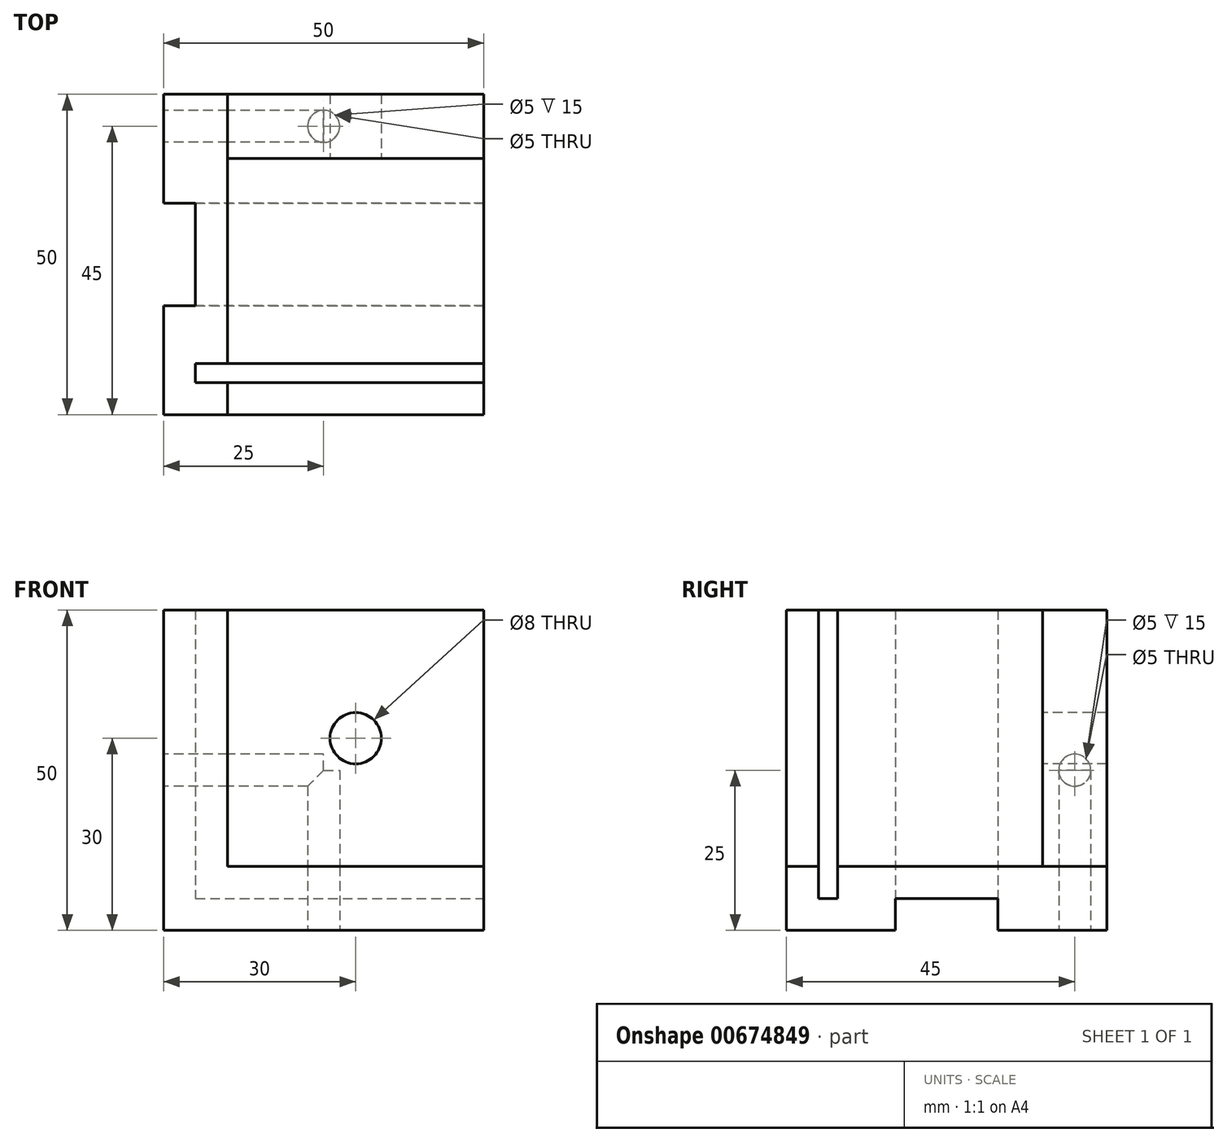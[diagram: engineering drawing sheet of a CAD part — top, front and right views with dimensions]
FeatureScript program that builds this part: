
annotation { "Feature Type Name" : "Feature", "Feature Type Description" : "" }
export const myFeature = defineFeature(function(context is Context, id is Id, definition is map)
    precondition{}
    {
        {
            var Q0;
            Q0=qCreatedBy(makeId("Front.planeOp"),FACE);
            var sketch = newSketch(context, id + "F0", { "sketchPlane" : qUnion([Q0])});
            skLineSegment(sketch, "E0", {"start": v(0, 0) * mm, "end": v(0, 50) * mm});
            skLineSegment(sketch, "E1", {"start": v(0, 50) * mm, "end": v(10, 50) * mm});
            skLineSegment(sketch, "E2", {"start": v(10, 50) * mm, "end": v(10, 10) * mm});
            skLineSegment(sketch, "E3", {"start": v(10, 10) * mm, "end": v(50, 10) * mm});
            skLineSegment(sketch, "E4", {"start": v(50, 10) * mm, "end": v(50, 0) * mm});
            skLineSegment(sketch, "E5", {"start": v(50, 0) * mm, "end": v(0, 0) * mm});
            skSolve(sketch);
        }
        {
            var Q0;
            Q0=makeQuery(id+"F0.imprint","IMPRINT",FACE,{"disambiguationData":[TD([[makeQuery(id+"F0.imprint","IMPRINT",EDGE,{"derivedFrom":sQuery(id+"F0.wireOp",EDGE,"E0")}),-1.0]])]});
            extrude(context, id + "F1", {"entities" : qUnion([Q0]), "depth" : 50 * mm, "offsetDistance" : 25 * mm});
        }
        {
            var Q0;
            Q0=makeQuery(id+"F1.opExtrude","SWEPT_FACE",FACE,{"disambiguationData":[OSD([sQuery(id+"F0.wireOp",EDGE,"E2")])]});
            var sketch = newSketch(context, id + "F2", { "sketchPlane" : qUnion([Q0])});
            skLineSegment(sketch, "E6", {"start": v(-45, 50) * mm, "end": v(-45, 10) * mm});
            skLineSegment(sketch, "E7", {"start": v(-45, 10) * mm, "end": v(-42, 10) * mm});
            skLineSegment(sketch, "E8", {"start": v(-42, 10) * mm, "end": v(-42, 50) * mm});
            skLineSegment(sketch, "E9", {"start": v(-45, 50) * mm, "end": v(-42, 50) * mm});
            skSolve(sketch);
        }
        {
            var Q0;
            Q0=makeQuery(id+"F2.imprint","IMPRINT",FACE,{"disambiguationData":[TD([[makeQuery(id+"F2.imprint","IMPRINT",EDGE,{"derivedFrom":sQuery(id+"F2.wireOp",EDGE,"E6")}),1.0]])]});
            extrude(context, id + "F3", {"entities" : qUnion([Q0]), "operationType" : NewBodyOperationType.REMOVE, "depth" : -5 * mm, "offsetDistance" : 25 * mm});
        }
        {
            var Q0;
            Q0=makeQuery(id+"F3.boolean.opBoolean","MERGE",FACE,{"derivedFrom":[makeQuery(id+"F1.opExtrude","SWEPT_FACE",FACE,{"disambiguationData":[OSD([sQuery(id+"F0.wireOp",EDGE,"E3")])]}),makeQuery(id+"F3.opExtrude","SWEPT_FACE",FACE,{"disambiguationData":[OSD([sQuery(id+"F2.wireOp",EDGE,"E7")])]})]});
            var sketch = newSketch(context, id + "F4", { "sketchPlane" : qUnion([Q0])});
            skLineSegment(sketch, "E10", {"start": v(10, -45) * mm, "end": v(50, -45) * mm});
            skLineSegment(sketch, "E11", {"start": v(50, -45) * mm, "end": v(50, -42) * mm});
            skLineSegment(sketch, "E12", {"start": v(50, -42) * mm, "end": v(10, -42) * mm});
            skSolve(sketch);
        }
        {
            var Q0;
            Q0=makeQuery(id+"F4.imprint","IMPRINT",FACE,{"disambiguationData":[TD([[makeQuery(id+"F4.imprint","IMPRINT",EDGE,{"derivedFrom":sQuery(id+"F4.wireOp",EDGE,"E10")}),1.0]])]});
            extrude(context, id + "F5", {"entities" : qUnion([Q0]), "operationType" : NewBodyOperationType.REMOVE, "oppositeDirection" : true, "depth" : 5 * mm, "offsetDistance" : 25 * mm});
        }
        {
            var Q0;
            Q0=makeQuery(id+"F1.opExtrude","CAP_FACE",FACE,{"disambiguationData":[OSD([sQuery(id+"F0.wireOp",EDGE,"E0"),sQuery(id+"F0.wireOp",EDGE,"E1"),sQuery(id+"F0.wireOp",EDGE,"E2"),sQuery(id+"F0.wireOp",EDGE,"E3"),sQuery(id+"F0.wireOp",EDGE,"E4"),sQuery(id+"F0.wireOp",EDGE,"E5")])],"isStart":true});
            var sketch = newSketch(context, id + "F6", { "sketchPlane" : qUnion([Q0])});
            skLineSegment(sketch, "E13", {"start": v(-10, 50) * mm, "end": v(-50, 50) * mm});
            skLineSegment(sketch, "E14", {"start": v(-50, 50) * mm, "end": v(-50, 10) * mm});
            skSolve(sketch);
        }
        {
            var Q0;
            Q0=makeQuery(id+"F6.imprint","IMPRINT",FACE,{"disambiguationData":[TD([[makeQuery(id+"F6.imprint","IMPRINT",EDGE,{"derivedFrom":sQuery(id+"F6.wireOp",EDGE,"E13")}),1.0]])]});
            extrude(context, id + "F7", {"entities" : qUnion([Q0]), "depth" : -10 * mm, "offsetDistance" : 25 * mm});
        }
        {
            var Q0;
            Q0=makeQuery(id+"F7.opExtrude","CAP_FACE",FACE,{"disambiguationData":[OSD([sQuery(id+"F0.wireOp",EDGE,"E2"),sQuery(id+"F0.wireOp",EDGE,"E3"),sQuery(id+"F6.wireOp",EDGE,"E13"),sQuery(id+"F6.wireOp",EDGE,"E14")])],"isStart":false});
            var sketch = newSketch(context, id + "F8", { "sketchPlane" : qUnion([Q0])});
            skLineSegment(sketch, "E15", {"start": v(10, 50) * mm, "end": v(50, 10) * mm, "construction": true});
            skLineSegment(sketch, "E16", {"start": v(50, 10) * mm, "end": v(50, 50) * mm, "construction": true});
            skLineSegment(sketch, "E17", {"start": v(50, 50) * mm, "end": v(10, 10) * mm, "construction": true});
            skCircle(sketch, "E18", {"center": v(30, 30) * mm, "radius": 4 * mm});
            skCircle(sketch, "E19", {"center": v(30, 30) * mm, "radius": 5 * mm});
            skSolve(sketch);
        }
        {
            var Q0;
            Q0=makeQuery(id+"F8.imprint","IMPRINT",FACE,{"disambiguationData":[TD([[makeQuery(id+"F8.imprint","IMPRINT",EDGE,{"derivedFrom":sQuery(id+"F8.wireOp",EDGE,"E18")}),1.0]])]});
            extrude(context, id + "F9", {"entities" : qUnion([Q0]), "operationType" : NewBodyOperationType.REMOVE, "oppositeDirection" : true, "depth" : 10 * mm, "offsetDistance" : 25 * mm});
        }
        {
            var Q0;
            Q0=makeQuery(id+"F1.opExtrude","SWEPT_FACE",FACE,{"disambiguationData":[OSD([sQuery(id+"F0.wireOp",EDGE,"E0")])]});
            var sketch = newSketch(context, id + "F10", { "sketchPlane" : qUnion([Q0])});
            skLineSegment(sketch, "E20", {"start": v(17, 50) * mm, "end": v(17, 0) * mm});
            skLineSegment(sketch, "E21", {"start": v(33, 50) * mm, "end": v(33, 0) * mm});
            skLineSegment(sketch, "E22", {"start": v(17, 50) * mm, "end": v(33, 50) * mm});
            skLineSegment(sketch, "E23", {"start": v(17, 0) * mm, "end": v(33, 0) * mm});
            skSolve(sketch);
        }
        {
            var Q0;
            Q0=makeQuery(id+"F10.imprint","IMPRINT",FACE,{"disambiguationData":[TD([[makeQuery(id+"F10.imprint","IMPRINT",EDGE,{"derivedFrom":sQuery(id+"F10.wireOp",EDGE,"E20")}),1.0]])]});
            extrude(context, id + "F11", {"entities" : qUnion([Q0]), "operationType" : NewBodyOperationType.REMOVE, "oppositeDirection" : true, "depth" : 5 * mm, "offsetDistance" : 25 * mm});
        }
        {
            var Q0;
            Q0=makeQuery(id+"F1.opExtrude","SWEPT_FACE",FACE,{"disambiguationData":[OSD([sQuery(id+"F0.wireOp",EDGE,"E5")])]});
            var sketch = newSketch(context, id + "F12", { "sketchPlane" : qUnion([Q0])});
            skLineSegment(sketch, "E24", {"start": v(5, 17) * mm, "end": v(50, 17) * mm});
            skLineSegment(sketch, "E25", {"start": v(5, 33) * mm, "end": v(50, 33) * mm});
            skLineSegment(sketch, "E26", {"start": v(50, 17) * mm, "end": v(50, 33) * mm});
            skSolve(sketch);
        }
        {
            var Q0;
            Q0 = qSketchRegion(id + "F12", true);
            var Q1;
            Q1=makeQuery(id+"F12.imprint","IMPRINT",FACE,{"disambiguationData":[TD([[makeQuery(id+"F12.imprint","IMPRINT",EDGE,{"derivedFrom":sQuery(id+"F12.wireOp",EDGE,"E24")}),1.0]])]});
            extrude(context, id + "F13", {"entities" : qUnion([Q0, Q1]), "operationType" : NewBodyOperationType.REMOVE, "oppositeDirection" : true, "depth" : 5 * mm, "offsetDistance" : 25 * mm});
        }
        {
            var Q0;
            {var subQ2=sQuery(id+"F0.wireOp",EDGE,"E0");Q0=makeQuery(id+"F11.boolean.opBoolean","SPLIT",FACE,{"disambiguationData":[TD([makeQuery(id+"F11.opExtrude","SWEPT_FACE",FACE,{"disambiguationData":[OSD([sQuery(id+"F10.wireOp",EDGE,"E20")])]})])],"derivedFrom":makeQuery(id+"F1.opExtrude","SWEPT_FACE",FACE,{"disambiguationData":[OSD([subQ2])]})});}
            var sketch = newSketch(context, id + "F14", { "sketchPlane" : qUnion([Q0])});
            skCircle(sketch, "E27", {"center": v(5, 25) * mm, "radius": 2.5 * mm});
            skSolve(sketch);
        }
        {
            var Q0;
            Q0=makeQuery(id+"F14.imprint","IMPRINT",FACE,{"disambiguationData":[TD([[makeQuery(id+"F14.imprint","IMPRINT",EDGE,{"derivedFrom":sQuery(id+"F14.wireOp",EDGE,"E27")}),1.0]])]});
            extrude(context, id + "F15", {"entities" : qUnion([Q0]), "operationType" : NewBodyOperationType.REMOVE, "oppositeDirection" : true, "depth" : 25 * mm, "offsetDistance" : 25 * mm});
        }
        {
            var Q0;
            {var subQ1=sQuery(id+"F0.wireOp",EDGE,"E5");Q0=makeQuery(id+"F13.boolean.opBoolean","SPLIT",FACE,{"disambiguationData":[TD([makeQuery(id+"F11.boolean.opBoolean","COPY",FACE,{"derivedFrom":makeQuery(id+"F11.opExtrude","SWEPT_FACE",FACE,{"disambiguationData":[OSD([sQuery(id+"F10.wireOp",EDGE,"E20")])]})})])],"derivedFrom":makeQuery(id+"F1.opExtrude","SWEPT_FACE",FACE,{"disambiguationData":[OSD([subQ1])]})});}
            var sketch = newSketch(context, id + "F16", { "sketchPlane" : qUnion([Q0])});
            skCircle(sketch, "E28", {"center": v(25, 5) * mm, "radius": 2.5 * mm});
            skSolve(sketch);
        }
        {
            var Q0;
            Q0=makeQuery(id+"F16.imprint","IMPRINT",FACE,{"disambiguationData":[TD([[makeQuery(id+"F16.imprint","IMPRINT",EDGE,{"derivedFrom":sQuery(id+"F16.wireOp",EDGE,"E28")}),1.0]])]});
            var Q1;
            Q1=sQuery(id+"F16.wireOp",EDGE,"E28");
            extrude(context, id + "F17", {"entities" : qUnion([Q0]), "operationType" : NewBodyOperationType.REMOVE, "surfaceEntities" : qUnion([Q1]), "depth" : -25 * mm, "offsetDistance" : 25 * mm});
        }
    });
